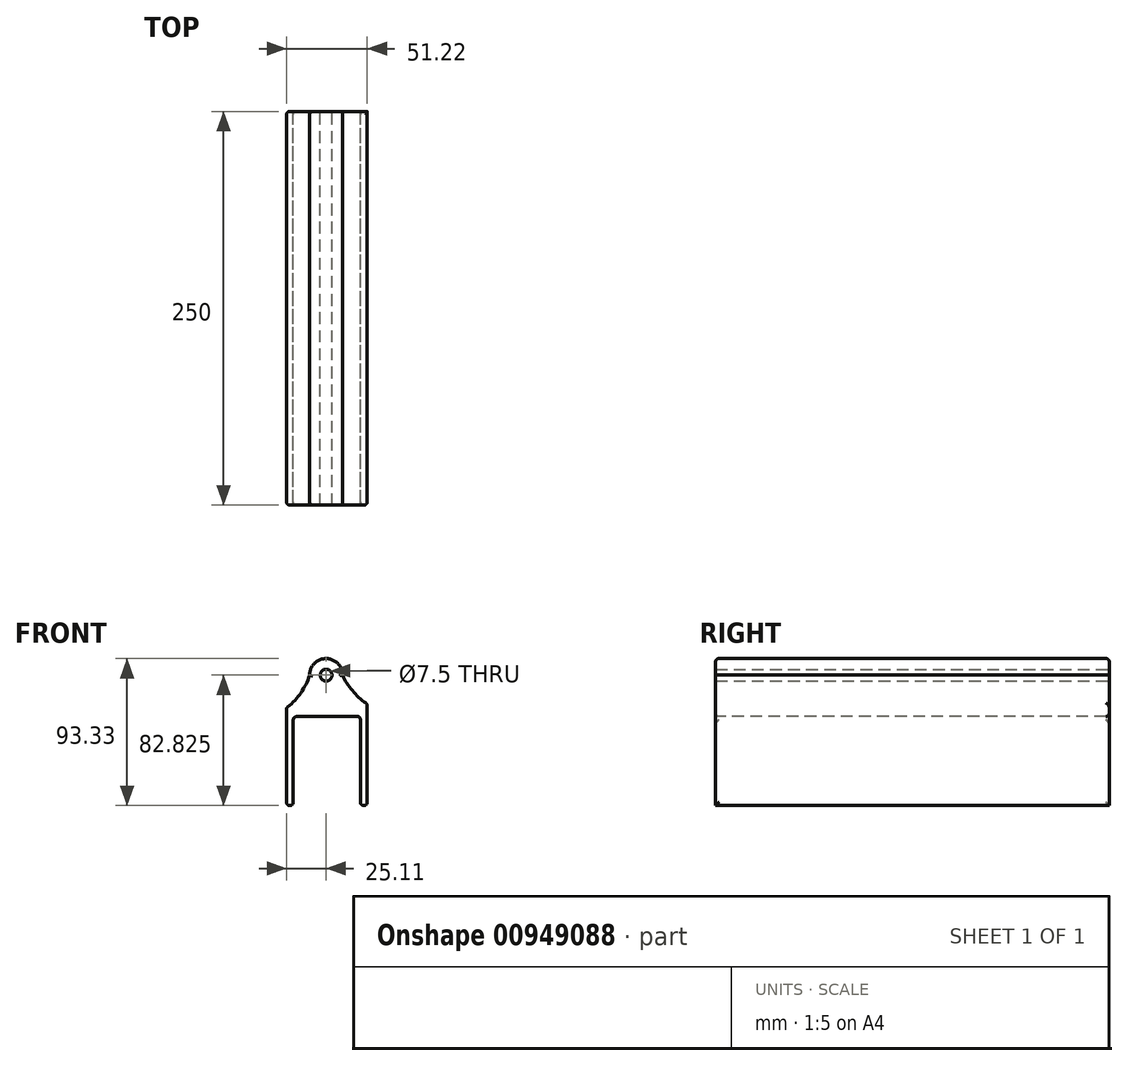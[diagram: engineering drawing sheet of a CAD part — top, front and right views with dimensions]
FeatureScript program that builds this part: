
annotation { "Feature Type Name" : "Feature", "Feature Type Description" : "" }
export const myFeature = defineFeature(function(context is Context, id is Id, definition is map)
    precondition{}
    {
        {
            var Q0;
            Q0=qCreatedBy(makeId("Front.planeOp"),FACE);
            var sketch = newSketch(context, id + "F0", { "sketchPlane" : qUnion([Q0])});
            skLineSegment(sketch, "E0.top", {"start": v(-25.1, -12.9) * mm, "end": v(-20.86, -12.9) * mm});
            skLineSegment(sketch, "E0.left", {"start": v(-25.1, 49.14) * mm, "end": v(-25.1, -12.9) * mm});
            skLineSegment(sketch, "E0.right", {"start": v(26.1, 51.54) * mm, "end": v(26.1, -12.9) * mm});
            skLineSegment(sketch, "E1.bottom", {"start": v(-20.86, 43.53) * mm, "end": v(-19.5, 43.53) * mm});
            skLineSegment(sketch, "E1.left", {"start": v(-20.86, 43.53) * mm, "end": v(-20.86, -12.9) * mm});
            skLineSegment(sketch, "E1.right", {"start": v(21.79, 43.75) * mm, "end": v(21.79, -12.9) * mm});
            skLineSegment(sketch, "E2.trimOffspring", {"start": v(21.79, -12.9) * mm, "end": v(26.1, -12.9) * mm});
            skLineSegment(sketch, "E3.trimOffspring", {"start": v(21.79, 43.75) * mm, "end": v(21.91, 43.75) * mm});
            skLineSegment(sketch, "E4", {"start": v(-19.5, 43.53) * mm, "end": v(21.91, 43.75) * mm});
            skArc(sketch, "E5", {"start": v(10.5, 69.93) * mm, "mid": v(-0.1, 80.44) * mm, "end": v(-10.5, 69.74) * mm});
            skArc(sketch, "E6", {"start": v(-25.1, 49.14) * mm, "mid": v(-16.25, 58.34) * mm, "end": v(-10.5, 69.74) * mm});
            skArc(sketch, "E7", {"start": v(10.5, 69.93) * mm, "mid": v(17.02, 59.64) * mm, "end": v(26.1, 51.54) * mm});
            skSolve(sketch);
        }
        {
            var Q0;
            Q0=makeQuery(id+"F0.imprint","IMPRINT",FACE,{"disambiguationData":[TD([[makeQuery(id+"F0.imprint","IMPRINT",EDGE,{"derivedFrom":sQuery(id+"F0.wireOp",EDGE,"E0.top")}),1.0]])]});
            var Q1;
            Q1 = qSketchRegion(id + "Fi1PHwEwRgzvEe9_1", true);
            extrude(context, id + "F1", {"entities" : qUnion([Q0, Q1]), "depth" : 250 * mm, "offsetDistance" : 25 * mm});
        }
        {
            var Q0;
            Q0=makeQuery(id+"F1.opExtrude","SWEPT_EDGE",EDGE,{"disambiguationData":[OSD([sQuery(id+"F0.wireOp",EDGE,"E0.right"),sQuery(id+"F0.wireOp",EDGE,"E7")])]});
            var Q1;
            Q1=makeQuery(id+"F1.opExtrude","SWEPT_EDGE",EDGE,{"disambiguationData":[OSD([sQuery(id+"F0.wireOp",EDGE,"E0.right"),sQuery(id+"F0.wireOp",EDGE,"E2.trimOffspring")])]});
            var Q2;
            Q2=makeQuery(id+"F1.opExtrude","SWEPT_EDGE",EDGE,{"disambiguationData":[OSD([sQuery(id+"F0.wireOp",EDGE,"E0.left"),sQuery(id+"F0.wireOp",EDGE,"E6")])]});
            var Q3;
            Q3=makeQuery(id+"F1.opExtrude","SWEPT_EDGE",EDGE,{"disambiguationData":[OSD([sQuery(id+"F0.wireOp",EDGE,"E0.top"),sQuery(id+"F0.wireOp",EDGE,"E0.left")])]});
            var Q4;
            Q4=makeQuery(id+"F1.opExtrude","SWEPT_EDGE",EDGE,{"disambiguationData":[OSD([sQuery(id+"F0.wireOp",EDGE,"E1.right"),sQuery(id+"F0.wireOp",EDGE,"E2.trimOffspring")])]});
            var Q5;
            Q5=makeQuery(id+"F1.opExtrude","SWEPT_EDGE",EDGE,{"disambiguationData":[OSD([sQuery(id+"F0.wireOp",EDGE,"E0.top"),sQuery(id+"F0.wireOp",EDGE,"E1.left")])]});
            var Q6;
            Q6=makeQuery(id+"F1.opExtrude","SWEPT_FACE",FACE,{"disambiguationData":[OSD([sQuery(id+"F0.wireOp",EDGE,"E1.bottom"),sQuery(id+"F0.wireOp",EDGE,"E4")])]});
            var Q7;
            Q7=makeQuery(id+"F1.opExtrude","CAP_EDGE",EDGE,{"disambiguationData":[OSD([sQuery(id+"F0.wireOp",EDGE,"E0.right")])],"isStart":false});
            var Q8;
            Q8=makeQuery(id+"F1.opExtrude","CAP_EDGE",EDGE,{"disambiguationData":[OSD([sQuery(id+"F0.wireOp",EDGE,"E7")])],"isStart":false});
            var Q9;
            Q9=makeQuery(id+"F1.opExtrude","CAP_EDGE",EDGE,{"disambiguationData":[OSD([sQuery(id+"F0.wireOp",EDGE,"E6")])],"isStart":false});
            var Q10;
            Q10=makeQuery(id+"F1.opExtrude","CAP_EDGE",EDGE,{"disambiguationData":[OSD([sQuery(id+"F0.wireOp",EDGE,"E5")])],"isStart":false});
            var Q11;
            Q11=makeQuery(id+"F1.opExtrude","CAP_EDGE",EDGE,{"disambiguationData":[OSD([sQuery(id+"F0.wireOp",EDGE,"E6")])],"isStart":true});
            var Q12;
            Q12=makeQuery(id+"F1.opExtrude","CAP_EDGE",EDGE,{"disambiguationData":[OSD([sQuery(id+"F0.wireOp",EDGE,"E7")])],"isStart":true});
            var Q13;
            Q13=makeQuery(id+"F1.opExtrude","CAP_EDGE",EDGE,{"disambiguationData":[OSD([sQuery(id+"F0.wireOp",EDGE,"E5")])],"isStart":true});
            var Q14;
            Q14=makeQuery(id+"F1.opExtrude","CAP_EDGE",EDGE,{"disambiguationData":[OSD([sQuery(id+"F0.wireOp",EDGE,"E0.left")])],"isStart":true});
            var Q15;
            Q15=makeQuery(id+"F1.opExtrude","CAP_EDGE",EDGE,{"disambiguationData":[OSD([sQuery(id+"F0.wireOp",EDGE,"E0.left")])],"isStart":false});
            fillet(context, id + "F2", {"entities" : qUnion([Q0, Q1, Q2, Q3, Q4, Q5, Q6, Q7, Q8, Q9, Q10, Q11, Q12, Q13, Q14, Q15]), "radius" : 2 * mm, "tangentPropagation" : true, "allowEdgeOverflow" : false});
        }
        {
            var Q0;
            Q0=sQuery(id+"F0.wireOp",VERTEX,"E5.center");
            var Q1;
            Q1=makeQuery(id+"F1.opExtrude","SWEPT_BODY",BODY,{"disambiguationData":[OSD([sQuery(id+"F0.wireOp",EDGE,"E0.top"),sQuery(id+"F0.wireOp",EDGE,"E0.left"),sQuery(id+"F0.wireOp",EDGE,"E0.right"),sQuery(id+"F0.wireOp",EDGE,"E1.bottom"),sQuery(id+"F0.wireOp",EDGE,"E1.left"),sQuery(id+"F0.wireOp",EDGE,"E1.right"),sQuery(id+"F0.wireOp",EDGE,"E2.trimOffspring"),sQuery(id+"F0.wireOp",EDGE,"E3.trimOffspring"),sQuery(id+"F0.wireOp",EDGE,"E4"),sQuery(id+"F0.wireOp",EDGE,"E5"),sQuery(id+"F0.wireOp",EDGE,"E6"),sQuery(id+"F0.wireOp",EDGE,"E7")])]});
            hole(context, id + "F3", {"style" : HoleStyle.SIMPLE, "endStyle" : HoleEndStyle.THROUGH, "oppositeDirection" : true, "holeDiameter" : 7.5 * mm, "majorDiameter" : 5 * mm, "isTappedThrough" : true, "tappedDepth" : 12 * mm, "tapClearance" : 3, "locations" : qUnion([Q0]), "scope" : qUnion([Q1])});
        }
    });
